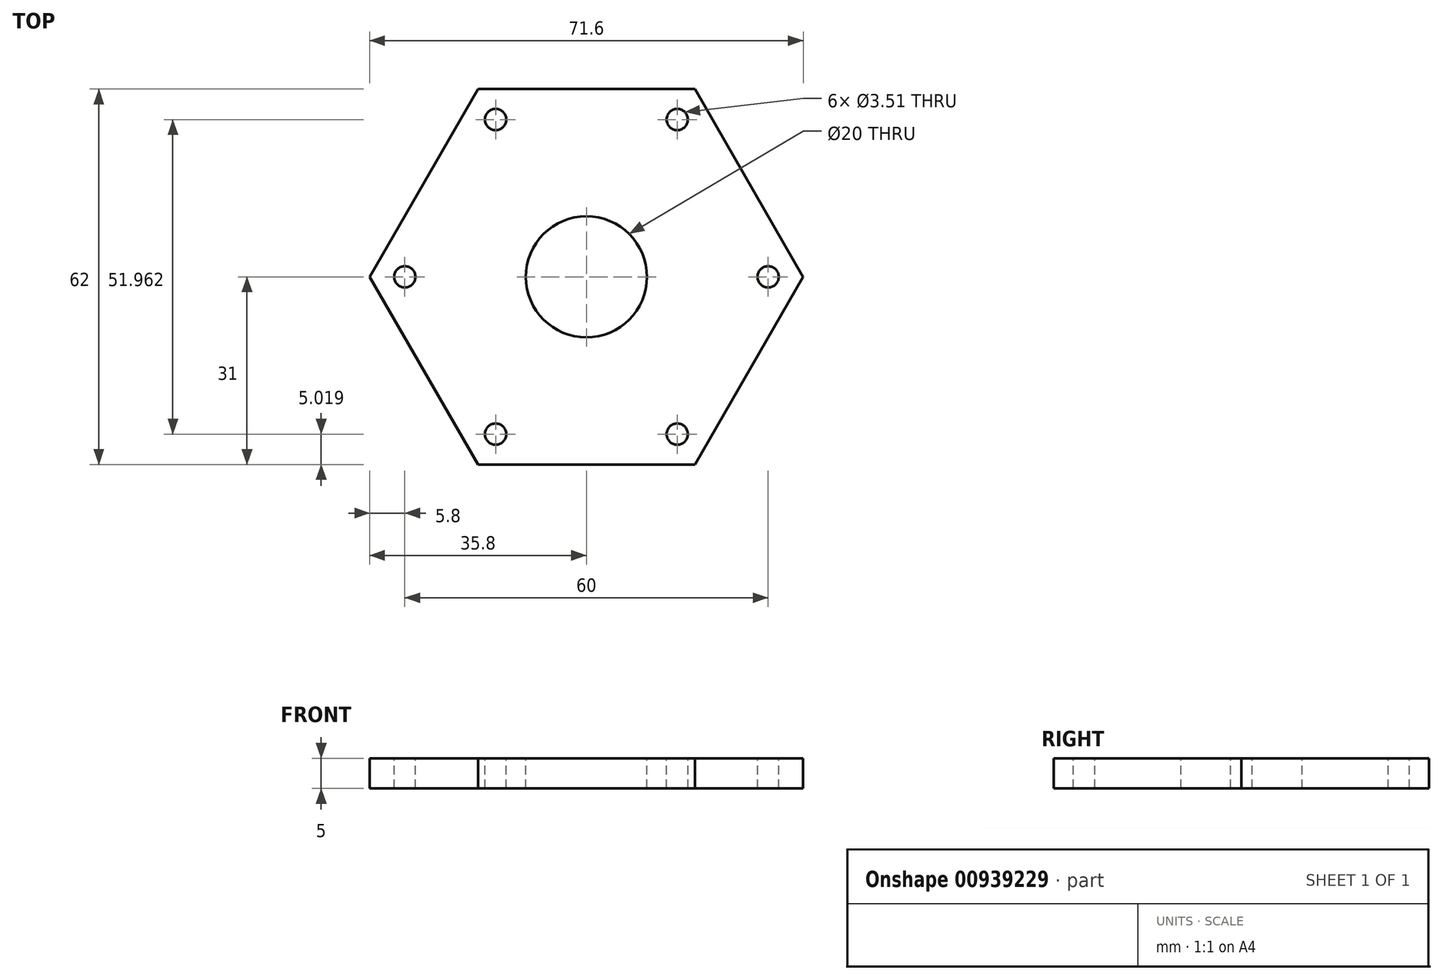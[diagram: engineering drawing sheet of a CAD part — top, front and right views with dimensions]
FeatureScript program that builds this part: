
annotation { "Feature Type Name" : "Feature", "Feature Type Description" : "" }
export const myFeature = defineFeature(function(context is Context, id is Id, definition is map)
    precondition{}
    {
        {
            var Q0;
            Q0=qCreatedBy(makeId("Top.planeOp"),FACE);
            var sketch = newSketch(context, id + "F0", { "sketchPlane" : qUnion([Q0])});
            skCircle(sketch, "E0.cCircle", {"center": v(0, 0) * mm, "radius": 31 * mm, "construction": true});
            skLineSegment(sketch, "E0.4", {"start": v(17.9, 31) * mm, "end": v(35.8, 0) * mm});
            skPoint(sketch, "E0.0.midPoint", {"position": v(0, -31) * mm});
            skLineSegment(sketch, "E1", {"start": v(0, 0) * mm, "end": v(17.9, 31) * mm});
            skLineSegment(sketch, "E2", {"start": v(0, 0) * mm, "end": v(17.9, -31) * mm});
            skLineSegment(sketch, "E3", {"start": v(35.8, 0) * mm, "end": v(17.9, -31) * mm});
            skSolve(sketch);
        }
        {
            var Q0;
            Q0=makeQuery(id+"F0.imprint","IMPRINT",FACE,{"disambiguationData":[TD([[makeQuery(id+"F0.imprint","IMPRINT",EDGE,{"derivedFrom":sQuery(id+"F0.wireOp",EDGE,"E0.4")}),-1.0]])]});
            extrude(context, id + "F1", {"entities" : qUnion([Q0]), "oppositeDirection" : true, "depth" : 5 * mm, "offsetDistance" : 25 * mm});
        }
        {
            var Q0;
            Q0=makeQuery(id+"F1.opExtrude","SWEPT_BODY",BODY,{"disambiguationData":[OSD([sQuery(id+"F0.wireOp",EDGE,"E0.4"),sQuery(id+"F0.wireOp",EDGE,"E1"),sQuery(id+"F0.wireOp",EDGE,"ICt1Kasn-KNWQ-kNFK-5hK5-lS0kEio0JAIP"),sQuery(id+"F0.wireOp",EDGE,"NNN5uVnY-U6ai-NDAJ-HlBG-4dcw1saHmlXd"),sQuery(id+"F0.wireOp",EDGE,"dM54E6H1-qOsS-v7i9-EFtR-accuUrwxJ4Pn")])]});
            var Q1;
            Q1=makeQuery(id+"F1.opExtrude","SWEPT_EDGE",EDGE,{"disambiguationData":[OSD([sQuery(id+"F0.wireOp",EDGE,"E1"),sQuery(id+"F0.wireOp",EDGE,"E2")])]});
            circularPattern(context, id + "F2", {"operationType" : NewBodyOperationType.ADD, "entities" : qUnion([Q0]), "axis" : qUnion([Q1]), "angle" : 360 * degree, "instanceCount" : 3, "equalSpace" : true});
        }
        {
            var Q0;
            {var subQ0=makeQuery(id+"F1.opExtrude","CAP_FACE",FACE,{"disambiguationData":[OSD([sQuery(id+"F0.wireOp",EDGE,"E0.4"),sQuery(id+"F0.wireOp",EDGE,"E1"),sQuery(id+"F0.wireOp",EDGE,"ICt1Kasn-KNWQ-kNFK-5hK5-lS0kEio0JAIP"),sQuery(id+"F0.wireOp",EDGE,"NNN5uVnY-U6ai-NDAJ-HlBG-4dcw1saHmlXd"),sQuery(id+"F0.wireOp",EDGE,"dM54E6H1-qOsS-v7i9-EFtR-accuUrwxJ4Pn")])],"isStart":true});Q0=makeQuery(id+"F2.boolean.opBoolean","MERGE",FACE,{"derivedFrom":[subQ0,makeQuery(id+"F2.opPattern","COPY",FACE,{"derivedFrom":subQ0,"instanceName":"1"}),makeQuery(id+"F2.opPattern","COPY",FACE,{"derivedFrom":subQ0,"instanceName":"2"}),makeQuery(id+"F2.opPattern","COPY",FACE,{"derivedFrom":subQ0,"instanceName":"3"}),makeQuery(id+"F2.opPattern","COPY",FACE,{"derivedFrom":subQ0,"instanceName":"4"}),makeQuery(id+"F2.opPattern","COPY",FACE,{"derivedFrom":subQ0,"instanceName":"5"})]});}
            var sketch = newSketch(context, id + "F3", { "sketchPlane" : qUnion([Q0])});
            skCircle(sketch, "E4", {"center": v(0, 0) * mm, "radius": 10 * mm});
            skLineSegment(sketch, "E5", {"start": v(-26.85, -15.5) * mm, "end": v(26.85, 15.5) * mm, "construction": true});
            skSolve(sketch);
        }
        {
            var Q0;
            Q0=makeQuery(id+"F3.imprint","IMPRINT",FACE,{"disambiguationData":[TD([[makeQuery(id+"F3.imprint","IMPRINT",EDGE,{"derivedFrom":sQuery(id+"F3.wireOp",EDGE,"E4")}),1.0]])]});
            var Q1;
            {var subQ0=makeQuery(id+"F1.opExtrude","CAP_FACE",FACE,{"disambiguationData":[OSD([sQuery(id+"F0.wireOp",EDGE,"E0.4"),sQuery(id+"F0.wireOp",EDGE,"E1"),sQuery(id+"F0.wireOp",EDGE,"ICt1Kasn-KNWQ-kNFK-5hK5-lS0kEio0JAIP"),sQuery(id+"F0.wireOp",EDGE,"NNN5uVnY-U6ai-NDAJ-HlBG-4dcw1saHmlXd"),sQuery(id+"F0.wireOp",EDGE,"dM54E6H1-qOsS-v7i9-EFtR-accuUrwxJ4Pn")])],"isStart":false});Q1=makeQuery(id+"F2.boolean.opBoolean","MERGE",FACE,{"derivedFrom":[subQ0,makeQuery(id+"F2.opPattern","COPY",FACE,{"derivedFrom":subQ0,"instanceName":"1"}),makeQuery(id+"F2.opPattern","COPY",FACE,{"derivedFrom":subQ0,"instanceName":"2"}),makeQuery(id+"F2.opPattern","COPY",FACE,{"derivedFrom":subQ0,"instanceName":"3"}),makeQuery(id+"F2.opPattern","COPY",FACE,{"derivedFrom":subQ0,"instanceName":"4"}),makeQuery(id+"F2.opPattern","COPY",FACE,{"derivedFrom":subQ0,"instanceName":"5"})]});}
            extrude(context, id + "F4", {"entities" : qUnion([Q0]), "operationType" : NewBodyOperationType.REMOVE, "endBound" : BoundingType.UP_TO_SURFACE, "oppositeDirection" : true, "depth" : 25 * mm, "endBoundEntityFace" : qUnion([Q1]), "offsetDistance" : 25 * mm});
        }
        {
            var Q0;
            {var subQ0=makeQuery(id+"F1.opExtrude","CAP_FACE",FACE,{"disambiguationData":[OSD([sQuery(id+"F0.wireOp",EDGE,"E0.4"),sQuery(id+"F0.wireOp",EDGE,"E1"),sQuery(id+"F0.wireOp",EDGE,"E2"),sQuery(id+"F0.wireOp",EDGE,"E3")])],"isStart":true});Q0=makeQuery(id+"F2.boolean.opBoolean","MERGE",FACE,{"derivedFrom":[subQ0,makeQuery(id+"F2.opPattern","COPY",FACE,{"derivedFrom":subQ0,"instanceName":"1"}),makeQuery(id+"F2.opPattern","COPY",FACE,{"derivedFrom":subQ0,"instanceName":"2"})]});}
            var sketch = newSketch(context, id + "F5", { "sketchPlane" : qUnion([Q0])});
            skCircle(sketch, "E6", {"center": v(15, 25.98) * mm, "radius": 1.76 * mm});
            skCircle(sketch, "E7", {"center": v(30, 0) * mm, "radius": 1.76 * mm});
            skCircle(sketch, "E8", {"center": v(15, -25.98) * mm, "radius": 1.76 * mm});
            skCircle(sketch, "E9", {"center": v(-15, -25.98) * mm, "radius": 1.76 * mm});
            skCircle(sketch, "E10", {"center": v(-30, 0) * mm, "radius": 1.76 * mm});
            skCircle(sketch, "E11", {"center": v(-15, 25.98) * mm, "radius": 1.76 * mm});
            skCircle(sketch, "E12.cCircle", {"center": v(0, 0) * mm, "radius": 25.98 * mm, "construction": true});
            skLineSegment(sketch, "E12.0", {"start": v(15, -25.98) * mm, "end": v(-15, -25.98) * mm, "construction": true});
            skLineSegment(sketch, "E12.1", {"start": v(-15, -25.98) * mm, "end": v(-30, 0) * mm, "construction": true});
            skLineSegment(sketch, "E12.2", {"start": v(-30, 0) * mm, "end": v(-15, 25.98) * mm, "construction": true});
            skLineSegment(sketch, "E12.3", {"start": v(-15, 25.98) * mm, "end": v(15, 25.98) * mm, "construction": true});
            skLineSegment(sketch, "E12.4", {"start": v(15, 25.98) * mm, "end": v(30, 0) * mm, "construction": true});
            skLineSegment(sketch, "E12.5", {"start": v(30, 0) * mm, "end": v(15, -25.98) * mm, "construction": true});
            skPoint(sketch, "E12.0.midPoint", {"position": v(0, -25.98) * mm});
            skSolve(sketch);
        }
        {
            var Q0;
            Q0=makeQuery(id+"F5.imprint","IMPRINT",FACE,{"disambiguationData":[TD([[makeQuery(id+"F5.imprint","IMPRINT",EDGE,{"derivedFrom":sQuery(id+"F5.wireOp",EDGE,"E8")}),1.0]])]});
            var Q1;
            Q1=makeQuery(id+"F5.imprint","IMPRINT",FACE,{"disambiguationData":[TD([[makeQuery(id+"F5.imprint","IMPRINT",EDGE,{"derivedFrom":sQuery(id+"F5.wireOp",EDGE,"E9")}),1.0]])]});
            var Q2;
            Q2=makeQuery(id+"F5.imprint","IMPRINT",FACE,{"disambiguationData":[TD([[makeQuery(id+"F5.imprint","IMPRINT",EDGE,{"derivedFrom":sQuery(id+"F5.wireOp",EDGE,"E7")}),1.0]])]});
            var Q3;
            Q3=makeQuery(id+"F5.imprint","IMPRINT",FACE,{"disambiguationData":[TD([[makeQuery(id+"F5.imprint","IMPRINT",EDGE,{"derivedFrom":sQuery(id+"F5.wireOp",EDGE,"E6")}),1.0]])]});
            var Q4;
            Q4=makeQuery(id+"F5.imprint","IMPRINT",FACE,{"disambiguationData":[TD([[makeQuery(id+"F5.imprint","IMPRINT",EDGE,{"derivedFrom":sQuery(id+"F5.wireOp",EDGE,"E11")}),1.0]])]});
            var Q5;
            Q5=makeQuery(id+"F5.imprint","IMPRINT",FACE,{"disambiguationData":[TD([[makeQuery(id+"F5.imprint","IMPRINT",EDGE,{"derivedFrom":sQuery(id+"F5.wireOp",EDGE,"E10")}),1.0]])]});
            var Q6;
            {var subQ0=makeQuery(id+"F1.opExtrude","CAP_FACE",FACE,{"disambiguationData":[OSD([sQuery(id+"F0.wireOp",EDGE,"E0.4"),sQuery(id+"F0.wireOp",EDGE,"E1"),sQuery(id+"F0.wireOp",EDGE,"E2"),sQuery(id+"F0.wireOp",EDGE,"E3")])],"isStart":false});Q6=makeQuery(id+"F2.boolean.opBoolean","MERGE",FACE,{"derivedFrom":[subQ0,makeQuery(id+"F2.opPattern","COPY",FACE,{"derivedFrom":subQ0,"instanceName":"1"}),makeQuery(id+"F2.opPattern","COPY",FACE,{"derivedFrom":subQ0,"instanceName":"2"})]});}
            extrude(context, id + "F6", {"entities" : qUnion([Q0, Q1, Q2, Q3, Q4, Q5]), "operationType" : NewBodyOperationType.REMOVE, "endBound" : BoundingType.UP_TO_SURFACE, "oppositeDirection" : true, "depth" : 25 * mm, "endBoundEntityFace" : qUnion([Q6]), "offsetDistance" : 25 * mm});
        }
    });
